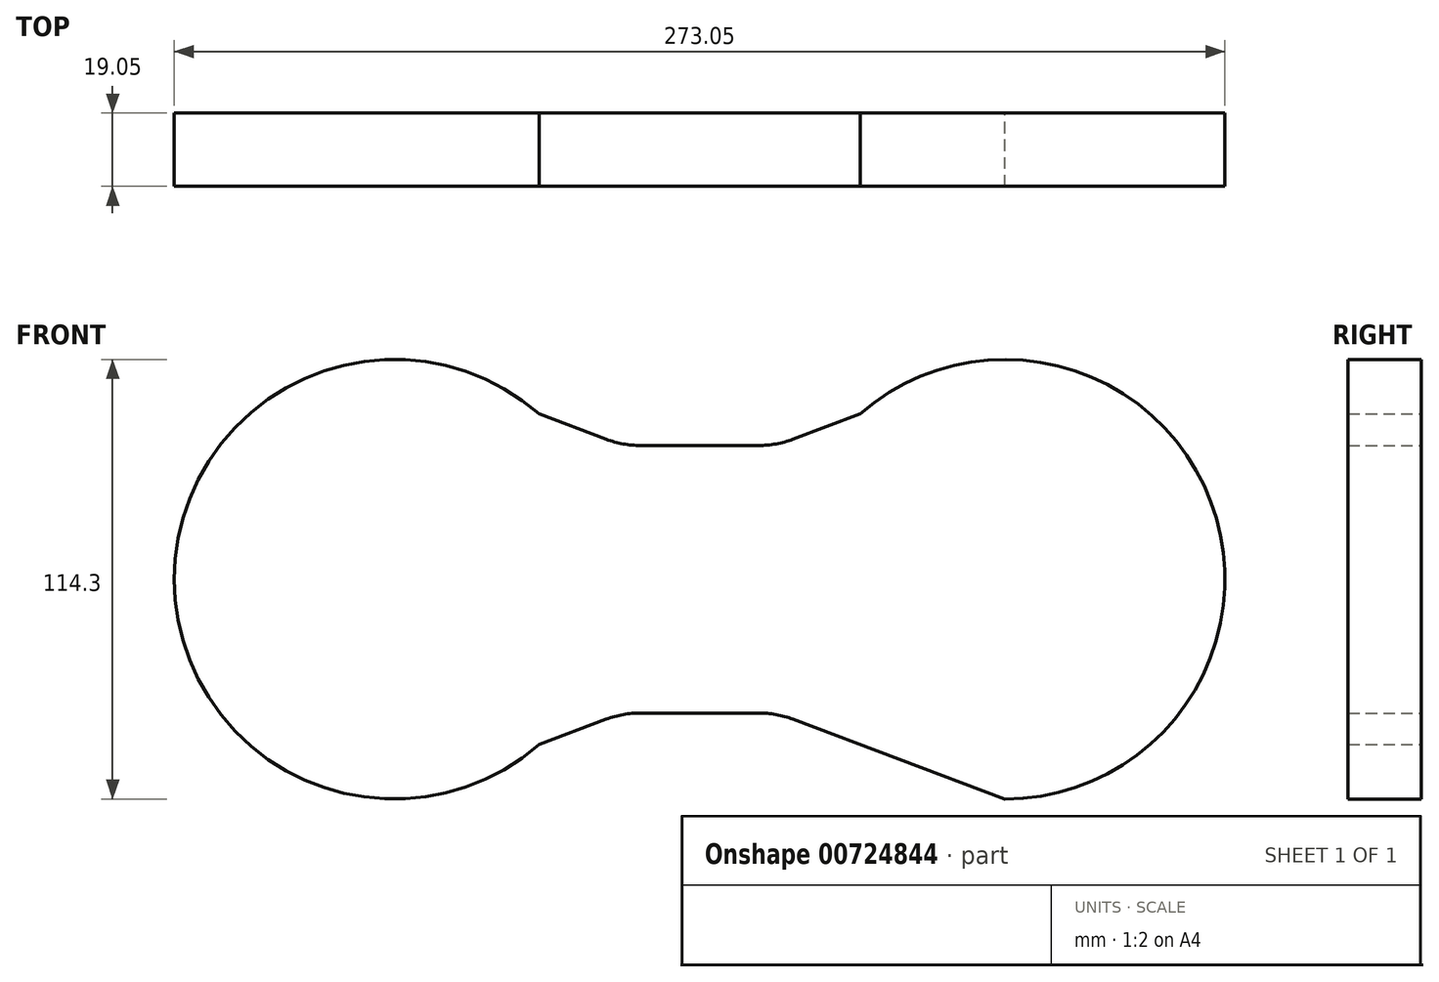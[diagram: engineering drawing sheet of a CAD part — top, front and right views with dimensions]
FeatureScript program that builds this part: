
annotation { "Feature Type Name" : "Feature", "Feature Type Description" : "" }
export const myFeature = defineFeature(function(context is Context, id is Id, definition is map)
    precondition{}
    {
        {
            var Q0;
            Q0=qCreatedBy(makeId("Front.planeOp"),FACE);
            var sketch = newSketch(context, id + "F0", { "sketchPlane" : qUnion([Q0])});
            skCircle(sketch, "E0", {"center": v(-35.08, 0) * mm, "radius": 57.15 * mm});
            skCircle(sketch, "E1", {"center": v(123.67, 0) * mm, "radius": 57.15 * mm});
            skLineSegment(sketch, "E2", {"start": v(-35.08, 57.15) * mm, "end": v(20.03, 36.4) * mm});
            skLineSegment(sketch, "E3", {"start": v(28.98, 34.78) * mm, "end": v(59.62, 34.78) * mm});
            skLineSegment(sketch, "E4", {"start": v(68.57, 36.4) * mm, "end": v(123.67, 57.15) * mm});
            skLineSegment(sketch, "E5", {"start": v(-35.08, -57.15) * mm, "end": v(20.03, -36.4) * mm});
            skLineSegment(sketch, "E6", {"start": v(28.98, -34.78) * mm, "end": v(59.62, -34.78) * mm});
            skLineSegment(sketch, "E7", {"start": v(68.57, -36.4) * mm, "end": v(123.67, -57.15) * mm});
            skPoint(sketch, "E8.visualSharp", {"position": v(24.35, 34.78) * mm});
            skArc(sketch, "E8.filletArc", {"start": v(20.03, 36.4) * mm, "mid": v(24.43, 35.19) * mm, "end": v(28.98, 34.78) * mm});
            skPoint(sketch, "E9.visualSharp", {"position": v(64.25, 34.78) * mm});
            skArc(sketch, "E9.filletArc", {"start": v(59.62, 34.78) * mm, "mid": v(64.17, 35.19) * mm, "end": v(68.57, 36.4) * mm});
            skPoint(sketch, "E10.visualSharp", {"position": v(24.35, -34.78) * mm});
            skArc(sketch, "E10.filletArc", {"start": v(28.98, -34.78) * mm, "mid": v(24.43, -35.19) * mm, "end": v(20.03, -36.4) * mm});
            skPoint(sketch, "E11.visualSharp", {"position": v(64.25, -34.78) * mm});
            skArc(sketch, "E11.filletArc", {"start": v(68.57, -36.4) * mm, "mid": v(64.17, -35.19) * mm, "end": v(59.62, -34.78) * mm});
            skSolve(sketch);
        }
        {
            var Q0;
            Q0=makeQuery(id+"F0.imprint","IMPRINT",FACE,{"disambiguationData":[TD([[makeQuery(id+"F0.imprint","IMPRINT",EDGE,{"derivedFrom":sQuery(id+"F0.wireOp",EDGE,"E3")}),-1.0]])]});
            var Q1;
            {var subQ0=sQuery(id+"F0.wireOp",EDGE,"E2");var subQ1=sQuery(id+"F0.wireOp",EDGE,"E0");var subQ2=makeQuery(id+"F0.imprint","INTERSECT",VERTEX,{"disambiguationData":[OD(0.0)],"derivedFrom":[subQ1,subQ0]});Q1=makeQuery(id+"F0.imprint","IMPRINT",FACE,{"disambiguationData":[TD([[makeQuery(id+"F0.imprint","IMPRINT",EDGE,{"disambiguationData":[TD([[subQ2,-1.0]])],"derivedFrom":subQ1}),1.0]])]});}
            var Q2;
            {var subQ0=sQuery(id+"F0.wireOp",EDGE,"E4");var subQ1=sQuery(id+"F0.wireOp",EDGE,"E1");var subQ2=makeQuery(id+"F0.imprint","INTERSECT",VERTEX,{"disambiguationData":[OD(1.0)],"derivedFrom":[subQ1,subQ0]});Q2=makeQuery(id+"F0.imprint","IMPRINT",FACE,{"disambiguationData":[TD([[makeQuery(id+"F0.imprint","IMPRINT",EDGE,{"disambiguationData":[TD([[subQ2,-1.0]])],"derivedFrom":subQ1}),1.0]])]});}
            var Q3;
            {var subQ0=sQuery(id+"F0.wireOp",EDGE,"E4");var subQ1=sQuery(id+"F0.wireOp",EDGE,"E1");var subQ2=makeQuery(id+"F0.imprint","INTERSECT",VERTEX,{"disambiguationData":[OD(0.0)],"derivedFrom":[subQ1,subQ0]});Q3=makeQuery(id+"F0.imprint","IMPRINT",FACE,{"disambiguationData":[TD([[makeQuery(id+"F0.imprint","IMPRINT",EDGE,{"disambiguationData":[TD([[subQ2,-1.0]])],"derivedFrom":subQ1}),1.0]])]});}
            var Q4;
            {var subQ0=sQuery(id+"F0.wireOp",EDGE,"E2");var subQ1=sQuery(id+"F0.wireOp",EDGE,"E0");var subQ2=makeQuery(id+"F0.imprint","INTERSECT",VERTEX,{"disambiguationData":[OD(0.0)],"derivedFrom":[subQ1,subQ0]});Q4=makeQuery(id+"F0.imprint","IMPRINT",FACE,{"disambiguationData":[TD([[makeQuery(id+"F0.imprint","IMPRINT",EDGE,{"disambiguationData":[TD([[subQ2,1.0]])],"derivedFrom":subQ1}),1.0]])]});}
            var Q5;
            {var subQ0=sQuery(id+"F0.wireOp",EDGE,"E5");var subQ1=sQuery(id+"F0.wireOp",EDGE,"E0");var subQ2=makeQuery(id+"F0.imprint","INTERSECT",VERTEX,{"disambiguationData":[OD(0.0)],"derivedFrom":[subQ1,subQ0]});Q5=makeQuery(id+"F0.imprint","IMPRINT",FACE,{"disambiguationData":[TD([[makeQuery(id+"F0.imprint","IMPRINT",EDGE,{"disambiguationData":[TD([[subQ2,-1.0]])],"derivedFrom":subQ1}),1.0]])]});}
            var Q6;
            {var subQ0=sQuery(id+"F0.wireOp",EDGE,"E7");var subQ1=sQuery(id+"F0.wireOp",EDGE,"E1");var subQ2=makeQuery(id+"F0.imprint","INTERSECT",VERTEX,{"disambiguationData":[OD(0.0)],"derivedFrom":[subQ1,subQ0]});Q6=makeQuery(id+"F0.imprint","IMPRINT",FACE,{"disambiguationData":[TD([[makeQuery(id+"F0.imprint","IMPRINT",EDGE,{"disambiguationData":[TD([[subQ2,1.0]])],"derivedFrom":subQ1}),1.0]])]});}
            extrude(context, id + "F1", {"entities" : qUnion([Q0, Q1, Q2, Q3, Q4, Q5, Q6]), "depth" : 19.05 * mm, "offsetDistance" : 25.4 * mm});
        }
    });
